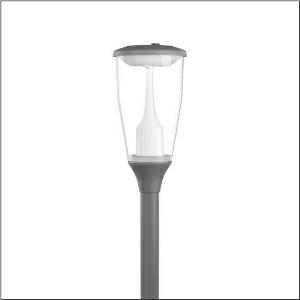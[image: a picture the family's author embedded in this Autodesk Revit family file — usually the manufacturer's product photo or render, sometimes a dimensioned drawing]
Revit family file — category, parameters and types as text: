
# Revit family: dl_11_iq___st1_2a_5xa5565ev14h000022_6439
name_source: partatom
category: Lighting Fixtures
units: mm (PartAtom-declared; Revit-internal decimal feet)

## family parameters
Cut with Voids When Loaded = No
Host = Face
Light Source = No
Part Type = Normal
Room Calculation Point = No
Round Connector Dimension = Use Diameter
Shared = No

## types (1)
- --- (1 x LED, 1560 lm, 10.7 W, 3000K)
    Apparent Load = 11 VA
    CIE Flux Codes = 24 63 94 96 100
    Color Rendering = 70
    Color Temperature = 3000K
    Default Elevation = 1800 mm
    Description = DL 11 iQ, mast luminaire, Module 540 iQ-SR, primary light control with 3 zone facetted reflector, of plastic, silver coated, highly specular, structured, primary optical cover: cover, of PMMA, transparent, light distribution: ST1.2a, light emission: direct distribution, primary light characteristic: asymmetric, installation type: post-top, LED, High Power LED, rated luminous flux: 1.560lm, luminous efficacy: 146lm/W, light colour: 730, colour temperature: 3000K, control gear: iQ-Street Remote, D4i with power reduction, control: pre-setting: logarithmic dimming characteristic, Street-Remote, Auto-Match, Temp-Guard, Lumen-Switch, Night-Set, Smart-Wire, Light-Fading, Desk-Remote (wireless, voltage-free reading and setting of iQ features in the workshop via application-optimized NFC function/RFID function), optimised constant luminous flux control (CLO 2.0), mains connection: 220..240V, AC, 50/60Hz, connection cable pre-assembled, cable length: 5,5m, start of lifetime: 11W, end of service life: 11W, reduction: 6W, luminaire housing, upper part, of diecast aluminium, coated, SITECO metallic grey (DB 702S), spigot size: 60mm (post-top), mounting height: 3..5m, post-top mast mounting element, of diecast aluminium, coated, SITECO metallic grey (DB 702S), Module 540 iQ-SR, traffic white (RAL 9016), equipment: standard, Smart Interface above, protection rating (complete): IP66, insulation class (complete): insulation class II (safety insulation), certification: CE, ENEC, ENEC+, VDE, impact resistance: IK07, packaging unit: 1 piece

Light Distribution: ST1.2a
    Height = 665 mm
    Lamp = 1 x LED
    Lamp Light Flux = 1560 lm
    Lamp Power = 10.7 W
    Lamp count = 1
    Length = 334 mm
    Luminous efficacy = 146 lm/W
    Manufacturer = Siteco
    ModVariant = No
    Model = 5XA5565EV14H000022
    Number of Poles = 1
    OnlyDefault = Yes
    Power Factor = 1
    Product Name = DL 11 iQ | ST1.2a
    Product group = mast luminaire | pylon top
    ProductGroupID = 6100
    Protection Class = Protection class II
    Protection Degree = IP 66
    RLX_Detail_Level = 1
    RLX_Emergency_Light_Flux = 0 lm
    RLX_Emergency_Type = 0
    RLX_Emergency_Type_DB = No
    RlxData = <blob elided: 154589 chars, md5=3c6c2812>
    Socket = socket
    Standby Power = 0 W
    System Light Flux = 1560 lm
    System Power = 11 W
    Type Comments = factory setting: luminous flux: 100 % | dim-lin: 254 | 419 mA
    Type Image = l_1337541.jpg
    URL = http://relux.com
    VarID = @adj_098961
    Voltage = 0 V
    Weight = 0.00 kg
    Width = 0 mm  [stored 0 ft]

note: [stored X ft] marks values corroborated as IEEE doubles in the binary element streams (Revit-internal decimal feet)

## geometry (parser evidence)
native form markers: Blend x4, Sweep x10
no freeform markers — native parametric forms only
